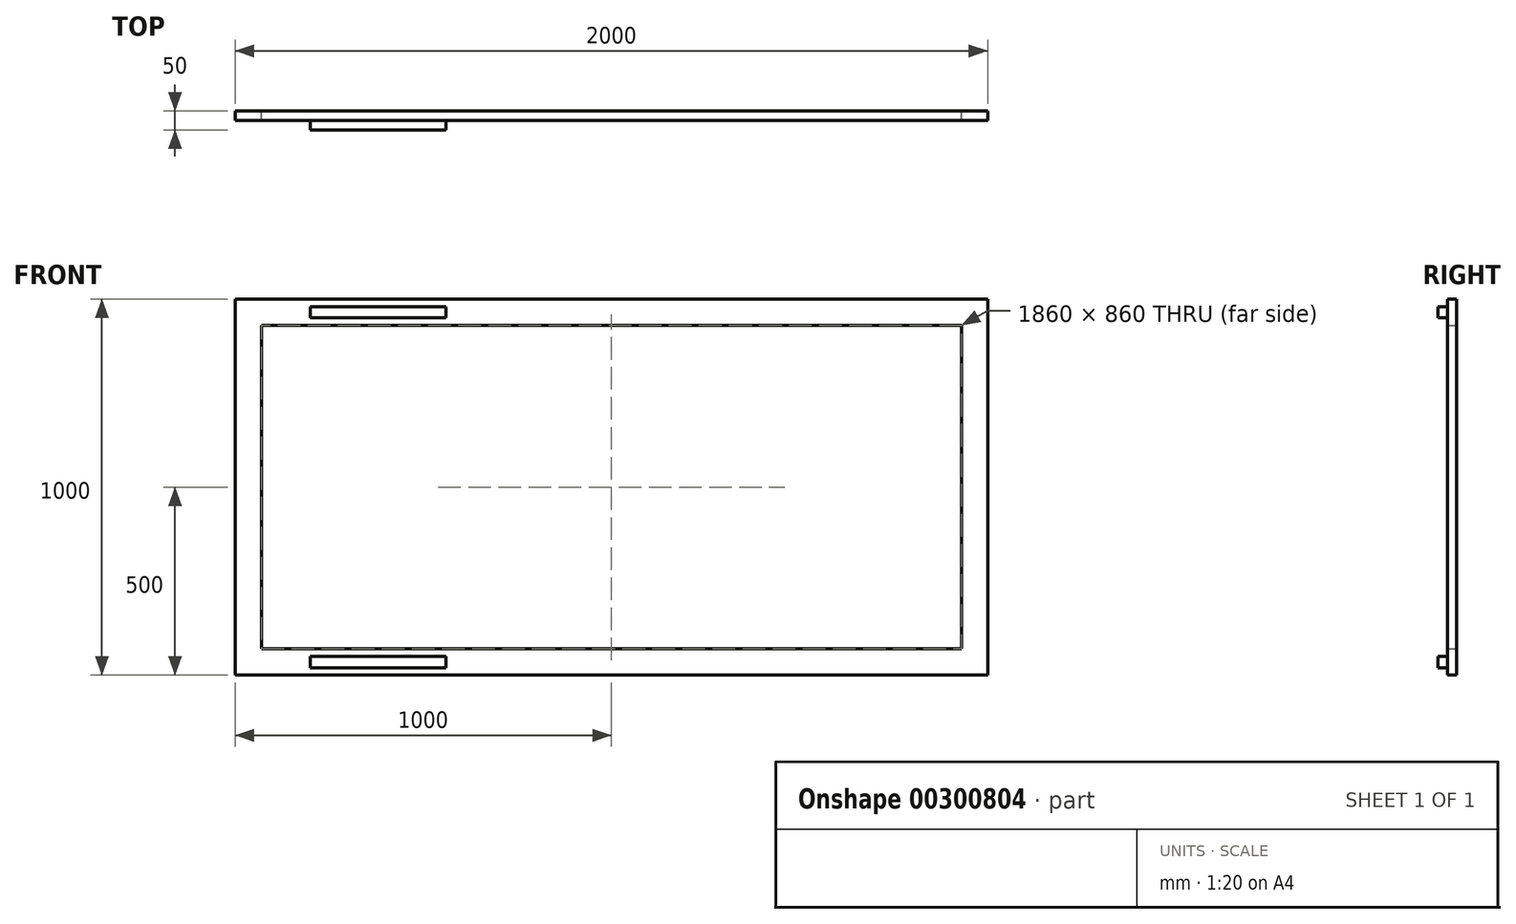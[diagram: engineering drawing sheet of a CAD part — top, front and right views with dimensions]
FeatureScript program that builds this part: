
annotation { "Feature Type Name" : "Feature", "Feature Type Description" : "" }
export const myFeature = defineFeature(function(context is Context, id is Id, definition is map)
    precondition{}
    {
        {
            var Q0;
            Q0=qCreatedBy(makeId("Front.planeOp"),FACE);
            var sketch = newSketch(context, id + "F0", { "sketchPlane" : qUnion([Q0])});
            skLineSegment(sketch, "E0.bottom", {"start": v(0, 0) * mm, "end": v(2000, 0) * mm});
            skLineSegment(sketch, "E0.top", {"start": v(0, -1000) * mm, "end": v(2000, -1000) * mm});
            skLineSegment(sketch, "E0.left", {"start": v(0, 0) * mm, "end": v(0, -1000) * mm});
            skLineSegment(sketch, "E0.right", {"start": v(2000, 0) * mm, "end": v(2000, -1000) * mm});
            skLineSegment(sketch, "E1.bottom", {"start": v(70, -70) * mm, "end": v(1930, -70) * mm});
            skLineSegment(sketch, "E1.top", {"start": v(70, -930) * mm, "end": v(1930, -930) * mm});
            skLineSegment(sketch, "E1.left", {"start": v(70, -70) * mm, "end": v(70, -930) * mm});
            skLineSegment(sketch, "E1.right", {"start": v(1930, -70) * mm, "end": v(1930, -930) * mm});
            skSolve(sketch);
        }
        {
            var Q0;
            Q0=makeQuery(id+"F0.imprint","IMPRINT",FACE,{"disambiguationData":[TD([[makeQuery(id+"F0.imprint","IMPRINT",EDGE,{"derivedFrom":sQuery(id+"F0.wireOp",EDGE,"E0.bottom")}),-1.0]])]});
            extrude(context, id + "F1", {"entities" : qUnion([Q0]), "depth" : 25 * mm});
        }
        {
            var Q0;
            Q0=makeQuery(id+"F1.opExtrude","CAP_FACE",FACE,{"disambiguationData":[OSD([sQuery(id+"F0.wireOp",EDGE,"E0.bottom"),sQuery(id+"F0.wireOp",EDGE,"E0.top"),sQuery(id+"F0.wireOp",EDGE,"E0.left"),sQuery(id+"F0.wireOp",EDGE,"E0.right"),sQuery(id+"F0.wireOp",EDGE,"E1.bottom"),sQuery(id+"F0.wireOp",EDGE,"E1.top"),sQuery(id+"F0.wireOp",EDGE,"E1.left"),sQuery(id+"F0.wireOp",EDGE,"E1.right")])],"isStart":false});
            var sketch = newSketch(context, id + "F2", { "sketchPlane" : qUnion([Q0])});
            skLineSegment(sketch, "E2.bottom", {"start": v(200, -20) * mm, "end": v(560, -20) * mm});
            skLineSegment(sketch, "E2.top", {"start": v(200, -50) * mm, "end": v(560, -50) * mm});
            skLineSegment(sketch, "E2.left", {"start": v(200, -20) * mm, "end": v(200, -50) * mm});
            skLineSegment(sketch, "E2.right", {"start": v(560, -20) * mm, "end": v(560, -50) * mm});
            skLineSegment(sketch, "E3.bottom", {"start": v(200, -950) * mm, "end": v(560, -950) * mm});
            skLineSegment(sketch, "E3.top", {"start": v(200, -980) * mm, "end": v(560, -980) * mm});
            skLineSegment(sketch, "E3.left", {"start": v(200, -950) * mm, "end": v(200, -980) * mm});
            skLineSegment(sketch, "E3.right", {"start": v(560, -950) * mm, "end": v(560, -980) * mm});
            skSolve(sketch);
        }
        {
            var Q0;
            Q0=makeQuery(id+"F2.imprint","IMPRINT",FACE,{"disambiguationData":[TD([[makeQuery(id+"F2.imprint","IMPRINT",EDGE,{"derivedFrom":sQuery(id+"F2.wireOp",EDGE,"E2.bottom")}),-1.0]])]});
            var Q1;
            Q1=makeQuery(id+"F2.imprint","IMPRINT",FACE,{"disambiguationData":[TD([[makeQuery(id+"F2.imprint","IMPRINT",EDGE,{"derivedFrom":sQuery(id+"F2.wireOp",EDGE,"E3.bottom")}),-1.0]])]});
            extrude(context, id + "F3", {"entities" : qUnion([Q0, Q1]), "operationType" : NewBodyOperationType.ADD, "depth" : 25 * mm});
        }
    });
